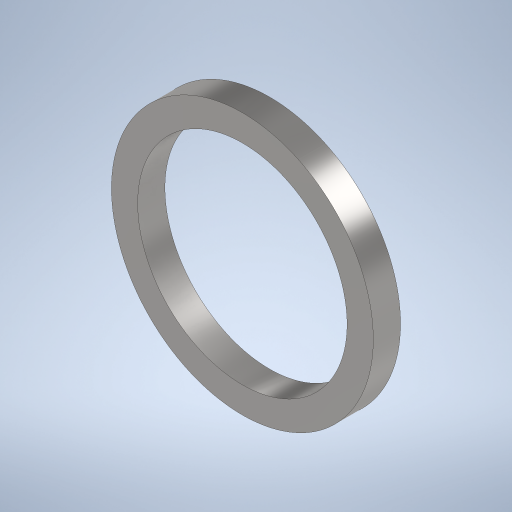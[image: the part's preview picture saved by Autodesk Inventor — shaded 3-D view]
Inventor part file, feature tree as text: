
AUTODESK INVENTOR PART (.ipt)
format: ipt  version: 2024 (Build 280153000, 153)  size: 236,032 bytes
history: native  units: mm
features: other x1, extrude x1, sketch x1
ambient origin geometry x8: Origin, YZ Plane, XZ Plane, XY Plane, X Axis, Y Axis, Z Axis, Center Point
bodies: Body1 (feature_tree)
feature tree (3):
  other  "ソリッド1"
  extrude  "押し出し1"  Depth=100.0mm
  sketch  "スケッチ1"
